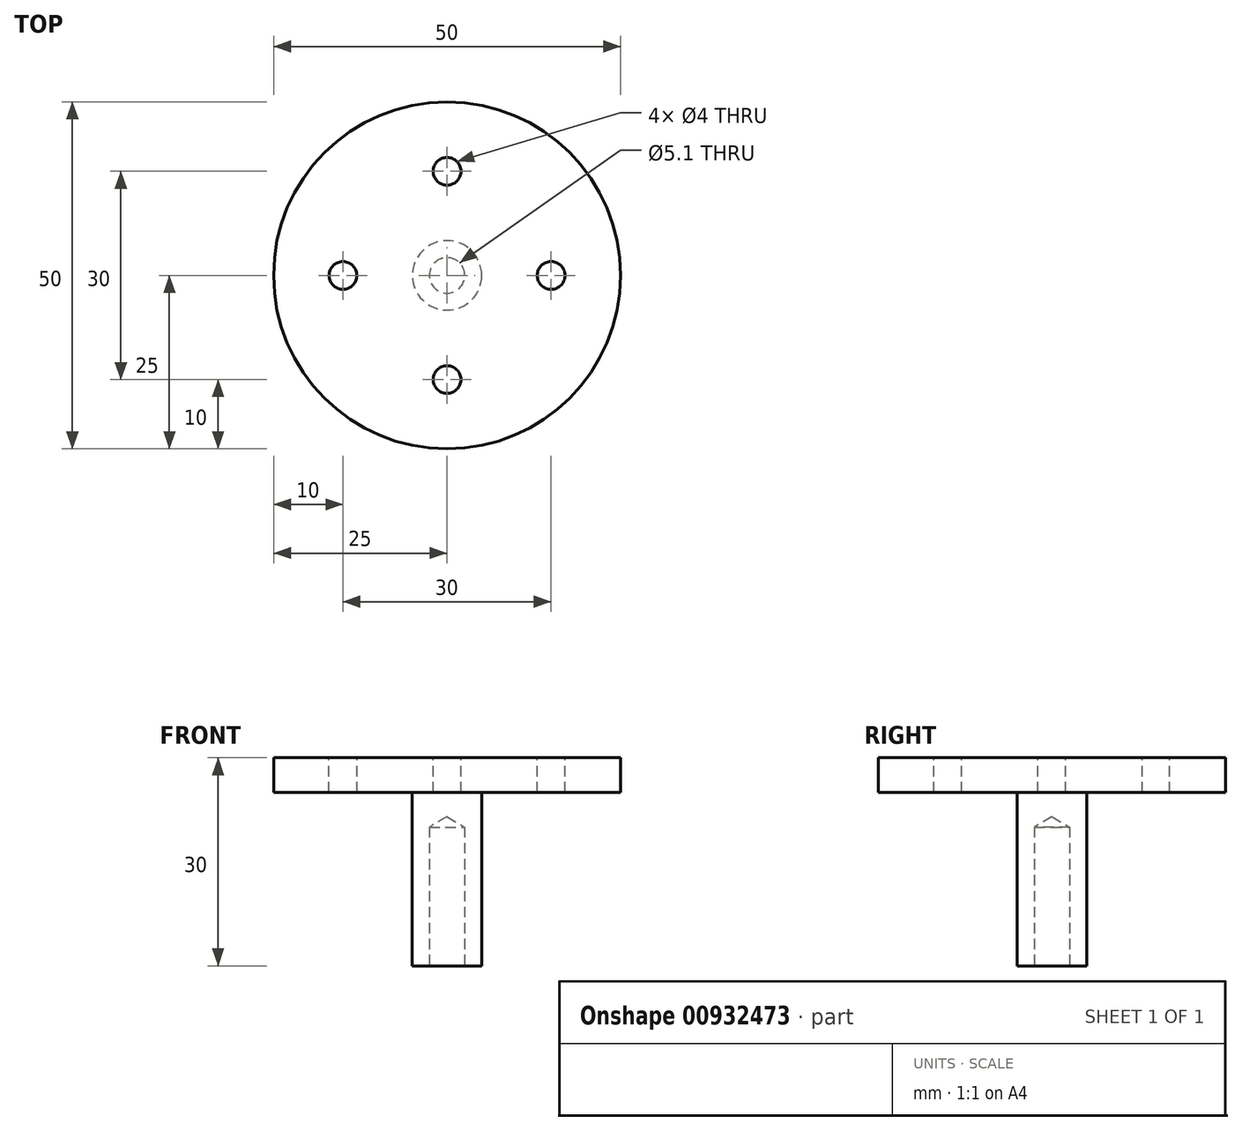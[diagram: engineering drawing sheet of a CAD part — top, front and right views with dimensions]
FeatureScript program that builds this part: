
annotation { "Feature Type Name" : "Feature", "Feature Type Description" : "" }
export const myFeature = defineFeature(function(context is Context, id is Id, definition is map)
    precondition{}
    {
        {
            var Q0;
            Q0=qCreatedBy(makeId("Top.planeOp"),FACE);
            var sketch = newSketch(context, id + "F0", { "sketchPlane" : qUnion([Q0])});
            skCircle(sketch, "E0", {"center": v(0, 0) * mm, "radius": 25 * mm});
            skSolve(sketch);
        }
        {
            var Q0;
            Q0=makeQuery(id+"F0.imprint","IMPRINT",FACE,{"disambiguationData":[TD([[makeQuery(id+"F0.imprint","IMPRINT",EDGE,{"derivedFrom":sQuery(id+"F0.wireOp",EDGE,"E0")}),1.0]])]});
            extrude(context, id + "F1", {"entities" : qUnion([Q0]), "depth" : 5 * mm, "offsetDistance" : 25 * mm});
        }
        {
            var Q0;
            Q0=makeQuery(id+"F1.opExtrude","CAP_FACE",FACE,{"disambiguationData":[OSD([sQuery(id+"F0.wireOp",EDGE,"E0")])],"isStart":true});
            var sketch = newSketch(context, id + "F2", { "sketchPlane" : qUnion([Q0])});
            skCircle(sketch, "E1", {"center": v(0, 0) * mm, "radius": 5 * mm});
            skSolve(sketch);
        }
        {
            var Q0;
            Q0=makeQuery(id+"F2.imprint","IMPRINT",FACE,{"disambiguationData":[TD([[makeQuery(id+"F2.imprint","IMPRINT",EDGE,{"derivedFrom":sQuery(id+"F2.wireOp",EDGE,"E1")}),1.0]])]});
            extrude(context, id + "F3", {"entities" : qUnion([Q0]), "operationType" : NewBodyOperationType.ADD, "depth" : 25 * mm, "offsetDistance" : 25 * mm});
        }
        {
            var Q0;
            Q0=makeQuery(id+"F3.opExtrude","CAP_FACE",FACE,{"disambiguationData":[OSD([sQuery(id+"F2.wireOp",EDGE,"E1")])],"isStart":false});
            var sketch = newSketch(context, id + "F4", { "sketchPlane" : qUnion([Q0])});
            skCircle(sketch, "E2", {"center": v(0, 0) * mm, "radius": 2.55 * mm});
            skSolve(sketch);
        }
        {
            var Q0;
            Q0=sQuery(id+"F4.wireOp",VERTEX,"E2.center");
            var Q1;
            Q1=makeQuery(id+"F1.opExtrude","SWEPT_BODY",BODY,{"disambiguationData":[OSD([sQuery(id+"F0.wireOp",EDGE,"E0")])]});
            hole(context, id + "F5", {"style" : HoleStyle.SIMPLE, "endStyle" : HoleEndStyle.BLIND, "holeDiameter" : 5.1 * mm, "majorDiameter" : 5 * mm, "holeDepth" : 20 * mm, "isTappedThrough" : true, "tappedDepth" : 12 * mm, "tapClearance" : 3, "startFromSketch" : true, "locations" : qUnion([Q0]), "scope" : qUnion([Q1])});
        }
        {
            var Q0;
            Q0=makeQuery(id+"F1.opExtrude","CAP_FACE",FACE,{"disambiguationData":[OSD([sQuery(id+"F0.wireOp",EDGE,"E0")])],"isStart":false});
            var sketch = newSketch(context, id + "F6", { "sketchPlane" : qUnion([Q0])});
            skLineSegment(sketch, "E3", {"start": v(0, 0) * mm, "end": v(0, 15) * mm});
            skLineSegment(sketch, "E4", {"start": v(0, 15) * mm, "end": v(0, -15) * mm});
            skLineSegment(sketch, "E5", {"start": v(0, 0) * mm, "end": v(15, 0) * mm});
            skLineSegment(sketch, "E6", {"start": v(15, 0) * mm, "end": v(-15, 0) * mm});
            skSolve(sketch);
        }
        {
            var Q0;
            Q0=sQuery(id+"F6.wireOp",VERTEX,"E3.end");
            var Q1;
            Q1=sQuery(id+"F6.wireOp",VERTEX,"E6.end");
            var Q2;
            Q2=sQuery(id+"F6.wireOp",VERTEX,"E4.end");
            var Q3;
            Q3=sQuery(id+"F6.wireOp",VERTEX,"E5.end");
            var Q4;
            Q4=makeQuery(id+"F1.opExtrude","SWEPT_BODY",BODY,{"disambiguationData":[OSD([sQuery(id+"F0.wireOp",EDGE,"E0")])]});
            hole(context, id + "F7", {"style" : HoleStyle.SIMPLE, "endStyle" : HoleEndStyle.BLIND, "holeDiameter" : 4 * mm, "majorDiameter" : 5 * mm, "holeDepth" : 20 * mm, "isTappedThrough" : true, "tappedDepth" : 12 * mm, "tapClearance" : 3, "startFromSketch" : true, "locations" : qUnion([Q0, Q1, Q2, Q3]), "scope" : qUnion([Q4])});
        }
    });
